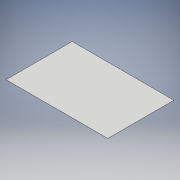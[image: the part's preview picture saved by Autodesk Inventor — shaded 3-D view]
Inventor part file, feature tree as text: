
AUTODESK INVENTOR PART (.ipt)
format: ipt  version: 2017 (Build 210142000, 142)  size: 93,696 bytes
history: native  units: mm
features: sheet_metal_op x1, sketch x1, other x1
ambient origin geometry x8: Origin, YZ Plane, XZ Plane, XY Plane, X Axis, Y Axis, Z Axis, Center Point
bodies: Solid1 (feature_tree)
feature tree (3):
  sheet_metal_op  "Face1"
  sketch  "Sketch1"  dims[d0=400.0mm d1=260.0mm d2=0.5mm]
  other  "Plate1"
